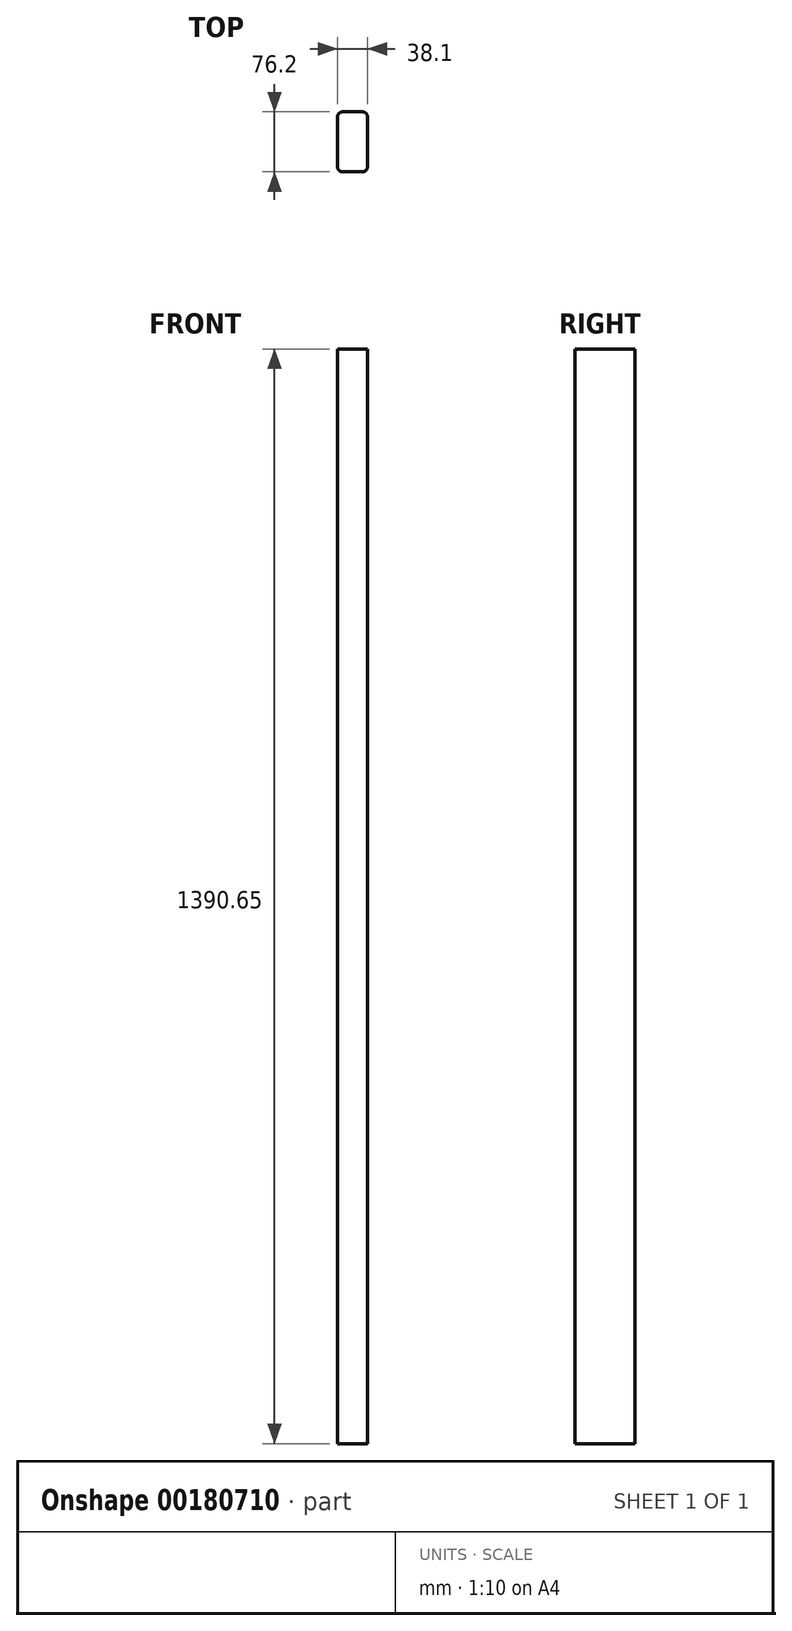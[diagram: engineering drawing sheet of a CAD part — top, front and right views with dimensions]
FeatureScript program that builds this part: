
annotation { "Feature Type Name" : "Feature", "Feature Type Description" : "" }
export const myFeature = defineFeature(function(context is Context, id is Id, definition is map)
    precondition{}
    {
        {
            var Q0;
            Q0=qCreatedBy(makeId("Top.planeOp"),FACE);
            var sketch = newSketch(context, id + "F0", { "sketchPlane" : qUnion([Q0])});
            skLineSegment(sketch, "E0.bottom", {"start": v(12.7, 38.1) * mm, "end": v(-12.7, 38.1) * mm});
            skLineSegment(sketch, "E0.top", {"start": v(12.7, -38.1) * mm, "end": v(-12.7, -38.1) * mm});
            skLineSegment(sketch, "E0.left", {"start": v(19.05, 31.75) * mm, "end": v(19.05, -31.75) * mm});
            skLineSegment(sketch, "E0.right", {"start": v(-19.05, 31.75) * mm, "end": v(-19.05, -31.75) * mm});
            skPoint(sketch, "E0.middle", {"position": v(0, 0) * mm});
            skPoint(sketch, "E1.visualSharp", {"position": v(19.05, -38.1) * mm});
            skArc(sketch, "E1.filletArc", {"start": v(12.7, -38.1) * mm, "mid": v(17.2, -36.24) * mm, "end": v(19.05, -31.75) * mm});
            skPoint(sketch, "E2.visualSharp", {"position": v(-19.05, -38.1) * mm});
            skArc(sketch, "E2.filletArc", {"start": v(-19.05, -31.75) * mm, "mid": v(-17.2, -36.24) * mm, "end": v(-12.7, -38.1) * mm});
            skPoint(sketch, "E3.visualSharp", {"position": v(-19.05, 38.1) * mm});
            skArc(sketch, "E3.filletArc", {"start": v(-12.7, 38.1) * mm, "mid": v(-17.2, 36.24) * mm, "end": v(-19.05, 31.75) * mm});
            skPoint(sketch, "E4.visualSharp", {"position": v(19.05, 38.1) * mm});
            skArc(sketch, "E4.filletArc", {"start": v(19.05, 31.75) * mm, "mid": v(17.2, 36.24) * mm, "end": v(12.7, 38.1) * mm});
            skSolve(sketch);
        }
        {
            var Q0;
            Q0 = qSketchRegion(id + "F0", true);
            extrude(context, id + "F1", {"entities" : qUnion([Q0]), "depth" : 1390.65 * mm});
        }
    });
